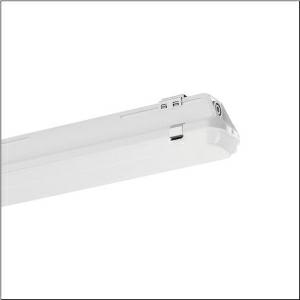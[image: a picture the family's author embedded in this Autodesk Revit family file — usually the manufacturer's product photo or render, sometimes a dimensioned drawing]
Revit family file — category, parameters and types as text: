
# Revit family: monsun_11_51fp10dp480l
name_source: partatom
category: Lighting Fixtures
units: mm (PartAtom-declared; Revit-internal decimal feet)

## family parameters
Cut with Voids When Loaded = No
Host = Face
Light Source = No
Part Type = Normal
Room Calculation Point = No
Round Connector Dimension = Use Diameter
Shared = No

## types (1)
- --- (1 x LED, 8000 lm, 44.4 W, 4000K)
    Apparent Load = 44 VA
    CIE Flux Codes = 47 77 93 94 100
    Color Rendering = 80
    Color Temperature = 4000K
    Default Elevation = 1800 mm
    Description = Monsun 11, damp-proof luminaire, chain hanger, primary optical cover: enclosure, of PMMA, light emission: direct distribution, primary light characteristic: symmetric, installation type: suspended mounting, surface-mounted, horizontal mounting, vertical mounting, LED, rated luminous flux: 8.000lm, luminous efficacy: 180lm/W, light colour: 840, colour temperature: 4000K, control gear: DALI 2, with terminal, 5-pole, max. 2.5mm², mains connection: 220..240V, AC, 50/60Hz, rated input power: 44W, luminaire housing, of glass-fibre reinforced polyester, uncoated, bright grey, incl. chain hanger, length: 1.590mm, width: 90mm, height: 88mm, clip for enclosure, of stainless steel (V2A), ceiling mounting element, of stainless steel (V2A), chain hanger, of stainless steel (V2A), protection rating (complete): IP66, insulation class (complete): insulation class I (protective earthing), certification: CE, ENEC, VDE, UKCA, protection symbol: D, impact resistance: IK04, permissible operating ambient temperature: -25..+30°C, standard: EN 50419, EN 60598-2-1, corresponds to IFS (International Featured Standards) requirements for safety and quality in the food industry, for indoor or canopied outdoor use, no direct snow, no direct sun, no direct rain, LABS conformity tested according to VDMA 24364:2018-05, contact your sales advisor before using the luminaires in applications with unclear chemical exposure, large temperature fluctuations or condensation-forming humidity, packaging unit: 1 piece
    Height = 89 mm
    Lamp = 1 x LED
    Lamp Light Flux = 8000 lm
    Lamp Power = 44.4 W
    Lamp count = 1
    Length = 1590 mm
    Luminous efficacy = 180 lm/W
    Manufacturer = Siteco
    ModVariant = No
    Model = 51FP10DP480L
    Mounting Place = Ceiling
    Mounting Type = Surface mounted
    Number of Poles = 1
    OnlyDefault = Yes
    Power Factor = 1
    Product Name = Monsun 11
    Product group = damp-proof luminaire
    ProductGroupID = 300
    Protection Class = Protection class I
    Protection Degree = IP 66
    RLX_Detail_Level = 1
    RLX_Emergency_Light_Flux = 0 lm
    RLX_Emergency_Type = 0
    RLX_Emergency_Type_DB = No
    RlxData = <blob elided: 91813 chars, md5=55f96c70>
    Socket = socket
    Standby Power = 0 W
    System Light Flux = 8000 lm
    System Power = 44 W
    Type Comments = factory setting: luminous flux: 100 % | dim-lin: 254 | 295 mA
    Type Image = l_1349237.jpg
    URL = http://relux.com
    VarID = @adj_033941
    Voltage = 0 V
    Weight = 0.00 kg
    Width = 90 mm

## geometry (parser evidence)
native form markers: Blend x4, Sweep x15
no freeform markers — native parametric forms only
